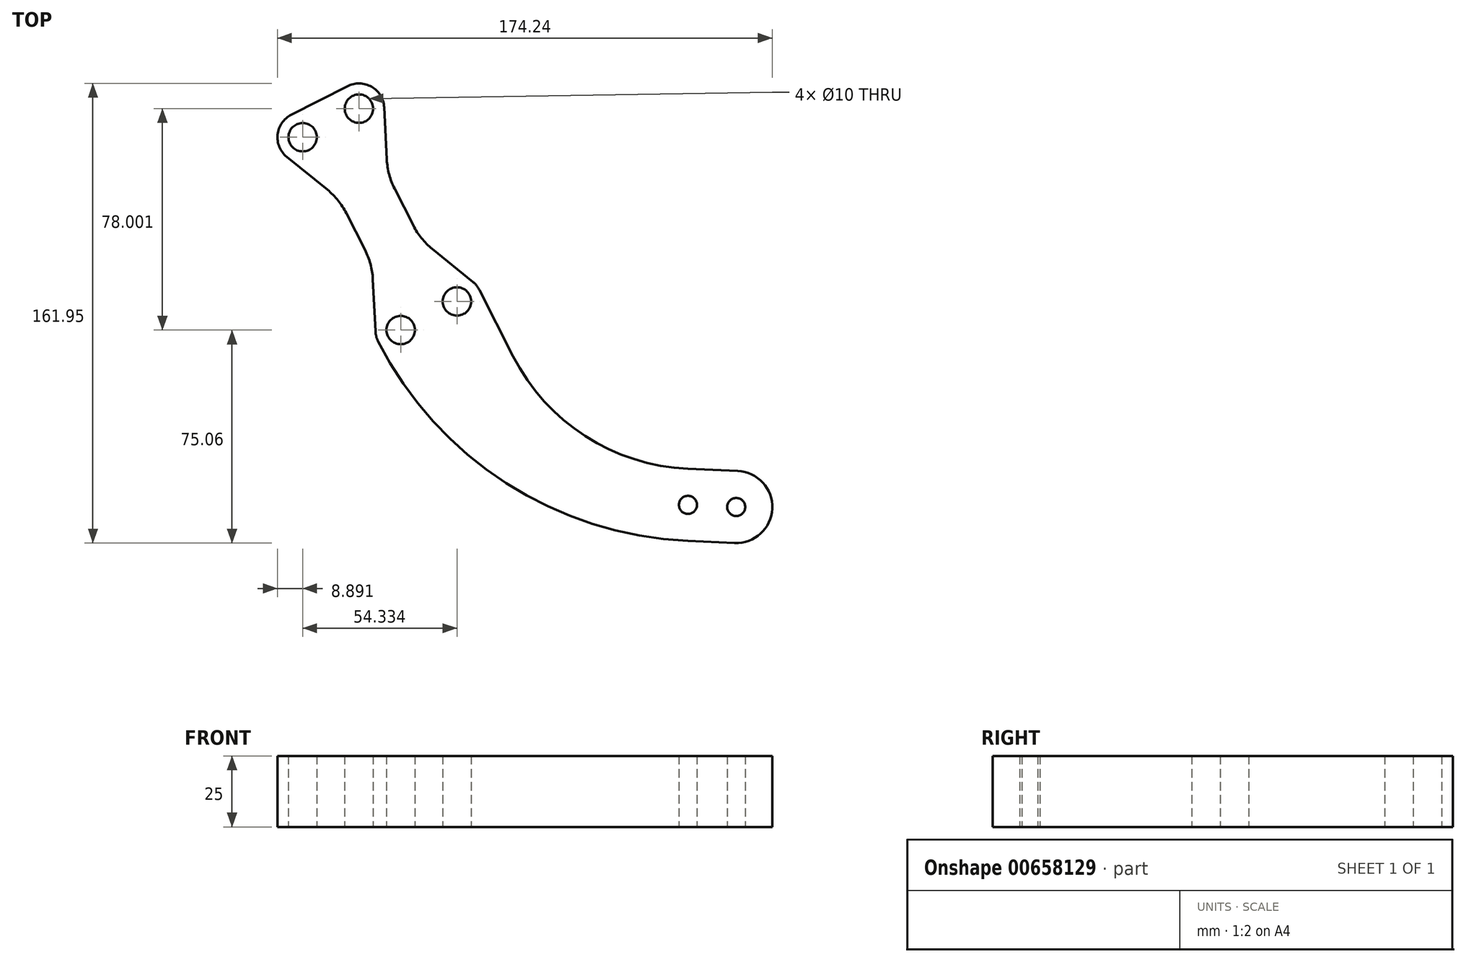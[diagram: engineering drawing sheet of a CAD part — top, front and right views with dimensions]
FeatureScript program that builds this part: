
annotation { "Feature Type Name" : "Feature", "Feature Type Description" : "" }
export const myFeature = defineFeature(function(context is Context, id is Id, definition is map)
    precondition{}
    {
        {
            var Q0;
            Q0=qCreatedBy(makeId("Top.planeOp"),FACE);
            var sketch = newSketch(context, id + "F0", { "sketchPlane" : qUnion([Q0])});
            skLineSegment(sketch, "E0", {"start": v(-108.86, 135.57) * mm, "end": v(-19.23, -40.81) * mm});
            skLineSegment(sketch, "E1", {"start": v(-55.74, 13.37) * mm, "end": v(-42.2, 20.75) * mm});
            skLineSegment(sketch, "E2", {"start": v(21.15, -7.36) * mm, "end": v(38.13, -8.12) * mm});
            skSolve(sketch);
        }
        {
            var Q0;
            Q0=qCreatedBy(makeId("Top.planeOp"),FACE);
            var sketch = newSketch(context, id + "F1", { "sketchPlane" : qUnion([Q0])});
            skCircle(sketch, "E3", {"center": v(21.15, -7.36) * mm, "radius": 3.18 * mm});
            skCircle(sketch, "E4", {"center": v(38.13, -8.12) * mm, "radius": 3.18 * mm});
            skLineSegment(sketch, "E5", {"start": v(-87.92, 50.21) * mm, "end": v(-126.47, 126.07) * mm});
            skLineSegment(sketch, "E6", {"start": v(-126.47, 126.07) * mm, "end": v(-90.8, 144.2) * mm});
            skLineSegment(sketch, "E7", {"start": v(-90.8, 144.2) * mm, "end": v(-40.42, 45.02) * mm});
            skLineSegment(sketch, "E8", {"start": v(-114.3, 132.25) * mm, "end": v(-42.64, -8.76) * mm, "construction": true});
            skLineSegment(sketch, "E9", {"start": v(-102.98, 138) * mm, "end": v(-31.32, -3) * mm, "construction": true});
            skLineSegment(sketch, "E10", {"start": v(-42.64, -8.76) * mm, "end": v(-31.32, -3) * mm, "construction": true});
            skPoint(sketch, "E11", {"position": v(-36.98, -5.88) * mm});
            skLineSegment(sketch, "E12", {"start": v(-42.64, -8.76) * mm, "end": v(-54.8, -14.94) * mm, "construction": true});
            skLineSegment(sketch, "E13", {"start": v(-31.32, -3) * mm, "end": v(-19.15, 3.18) * mm, "construction": true});
            skCircle(sketch, "E14", {"center": v(-80, 54.24) * mm, "radius": 5 * mm});
            skCircle(sketch, "E15", {"center": v(-60.18, 64.3) * mm, "radius": 5 * mm});
            skCircle(sketch, "E16", {"center": v(-114.52, 122.17) * mm, "radius": 5 * mm});
            skCircle(sketch, "E17", {"center": v(-94.7, 132.24) * mm, "radius": 5 * mm});
            skLineSegment(sketch, "E18", {"start": v(-114.52, 122.17) * mm, "end": v(-94.7, 132.24) * mm, "construction": true});
            skLineSegment(sketch, "E19", {"start": v(-80, 54.24) * mm, "end": v(-60.18, 64.3) * mm, "construction": true});
            skPoint(sketch, "E20", {"position": v(-70.1, 59.27) * mm});
            skPoint(sketch, "E21", {"position": v(-104.61, 127.2) * mm});
            skLineSegment(sketch, "E22", {"start": v(-60.18, 64.3) * mm, "end": v(-52.26, 68.34) * mm, "construction": true});
            skPoint(sketch, "E23.visualSharp", {"position": v(-19.15, 3.18) * mm});
            skArc(sketch, "E23.filletArc", {"start": v(-40.42, 45.02) * mm, "mid": v(-15, 16.86) * mm, "end": v(21.15, 5.35) * mm});
            skPoint(sketch, "E24.visualSharp", {"position": v(-52.2, -20.06) * mm});
            skArc(sketch, "E24.filletArc", {"start": v(-87.92, 50.21) * mm, "mid": v(-42.89, 0.32) * mm, "end": v(21.15, -20.08) * mm});
            skLineSegment(sketch, "E25", {"start": v(-87.92, 50.21) * mm, "end": v(-84.46, 51.98) * mm, "construction": true});
            skLineSegment(sketch, "E26", {"start": v(-116.78, 126.63) * mm, "end": v(-118.55, 130.1) * mm, "construction": true});
            skLineSegment(sketch, "E27", {"start": v(21.15, -7.36) * mm, "end": v(38.13, -8.12) * mm, "construction": true});
            skLineSegment(sketch, "E28", {"start": v(21.15, 5.35) * mm, "end": v(38.7, 4.57) * mm});
            skLineSegment(sketch, "E29", {"start": v(21.15, -20.08) * mm, "end": v(37.57, -20.8) * mm});
            skLineSegment(sketch, "E30", {"start": v(38.7, 4.57) * mm, "end": v(37.57, -20.8) * mm, "construction": true});
            skArc(sketch, "E31", {"start": v(37.57, -20.8) * mm, "mid": v(50.82, -8.68) * mm, "end": v(38.7, 4.57) * mm});
            skPoint(sketch, "E32", {"position": v(-87.35, 93.24) * mm});
            skLineSegment(sketch, "E33", {"start": v(-70.1, 59.27) * mm, "end": v(-104.61, 127.2) * mm, "construction": true});
            skCircle(sketch, "E34", {"center": v(-114.52, 122.17) * mm, "radius": 8.89 * mm});
            skCircle(sketch, "E35", {"center": v(-94.7, 132.24) * mm, "radius": 8.89 * mm});
            skCircle(sketch, "E36", {"center": v(-80, 54.24) * mm, "radius": 8.89 * mm});
            skCircle(sketch, "E37", {"center": v(-60.18, 64.3) * mm, "radius": 8.89 * mm});
            skLineSegment(sketch, "E38", {"start": v(-73.1, 86.23) * mm, "end": v(-54.59, 71.21) * mm});
            skLineSegment(sketch, "E39", {"start": v(-90.09, 77.6) * mm, "end": v(-88.87, 53.79) * mm});
            skLineSegment(sketch, "E40", {"start": v(-101.6, 100.25) * mm, "end": v(-120.12, 115.27) * mm});
            skLineSegment(sketch, "E41", {"start": v(-84.61, 108.88) * mm, "end": v(-85.83, 132.7) * mm});
            skLineSegment(sketch, "E42", {"start": v(-101.6, 100.25) * mm, "end": v(-84.61, 108.88) * mm, "construction": true});
            skLineSegment(sketch, "E43", {"start": v(-93.01, 90.36) * mm, "end": v(-87.35, 93.24) * mm});
            skLineSegment(sketch, "E44", {"start": v(-101.6, 100.25) * mm, "end": v(-90.09, 77.6) * mm});
            skLineSegment(sketch, "E45", {"start": v(-84.61, 108.88) * mm, "end": v(-73.1, 86.23) * mm});
            skLineSegment(sketch, "E46", {"start": v(-90.09, 77.6) * mm, "end": v(-73.1, 86.23) * mm, "construction": true});
            skSolve(sketch);
        }
        {
            var Q0;
            Q0=makeQuery(id+"F1.imprint","IMPRINT",FACE,{"disambiguationData":[TD([[makeQuery(id+"F1.imprint","IMPRINT",EDGE,{"derivedFrom":sQuery(id+"F1.wireOp",EDGE,"E3")}),-1.0]])]});
            var Q1;
            Q1=makeQuery(id+"F1.imprint","IMPRINT",FACE,{"disambiguationData":[TD([[makeQuery(id+"F1.imprint","IMPRINT",EDGE,{"derivedFrom":sQuery(id+"F1.wireOp",EDGE,"E16")}),-1.0]])]});
            var Q2;
            Q2=makeQuery(id+"F1.imprint","IMPRINT",FACE,{"disambiguationData":[TD([[makeQuery(id+"F1.imprint","IMPRINT",EDGE,{"derivedFrom":sQuery(id+"F1.wireOp",EDGE,"E17")}),-1.0]])]});
            var Q3;
            Q3=makeQuery(id+"F1.imprint","IMPRINT",FACE,{"disambiguationData":[TD([[makeQuery(id+"F1.imprint","IMPRINT",EDGE,{"derivedFrom":sQuery(id+"F1.wireOp",EDGE,"E14")}),-1.0]])]});
            var Q4;
            Q4=makeQuery(id+"F1.imprint","IMPRINT",FACE,{"disambiguationData":[TD([[makeQuery(id+"F1.imprint","IMPRINT",EDGE,{"derivedFrom":sQuery(id+"F1.wireOp",EDGE,"E15")}),-1.0]])]});
            extrude(context, id + "F2", {"entities" : qUnion([Q0, Q1, Q2, Q3, Q4]), "depth" : 25 * mm, "offsetDistance" : 25 * mm});
        }
        {
            var Q0;
            Q0=makeQuery(id+"F2.opExtrude","SWEPT_EDGE",EDGE,{"disambiguationData":[OSD([sQuery(id+"F1.wireOp",EDGE,"E38"),sQuery(id+"F1.wireOp",EDGE,"E45")])]});
            var Q1;
            Q1=makeQuery(id+"F2.opExtrude","SWEPT_EDGE",EDGE,{"disambiguationData":[OSD([sQuery(id+"F1.wireOp",EDGE,"E41"),sQuery(id+"F1.wireOp",EDGE,"E45")])]});
            var Q2;
            Q2=makeQuery(id+"F2.opExtrude","SWEPT_EDGE",EDGE,{"disambiguationData":[OSD([sQuery(id+"F1.wireOp",EDGE,"E40"),sQuery(id+"F1.wireOp",EDGE,"E44")])]});
            var Q3;
            Q3=makeQuery(id+"F2.opExtrude","SWEPT_EDGE",EDGE,{"disambiguationData":[OSD([sQuery(id+"F1.wireOp",EDGE,"E39"),sQuery(id+"F1.wireOp",EDGE,"E44")])]});
            fillet(context, id + "F3", {"entities" : qUnion([Q0, Q1, Q2, Q3]), "radius" : 25.4 * mm, "tangentPropagation" : true, "allowEdgeOverflow" : false});
        }
    });
